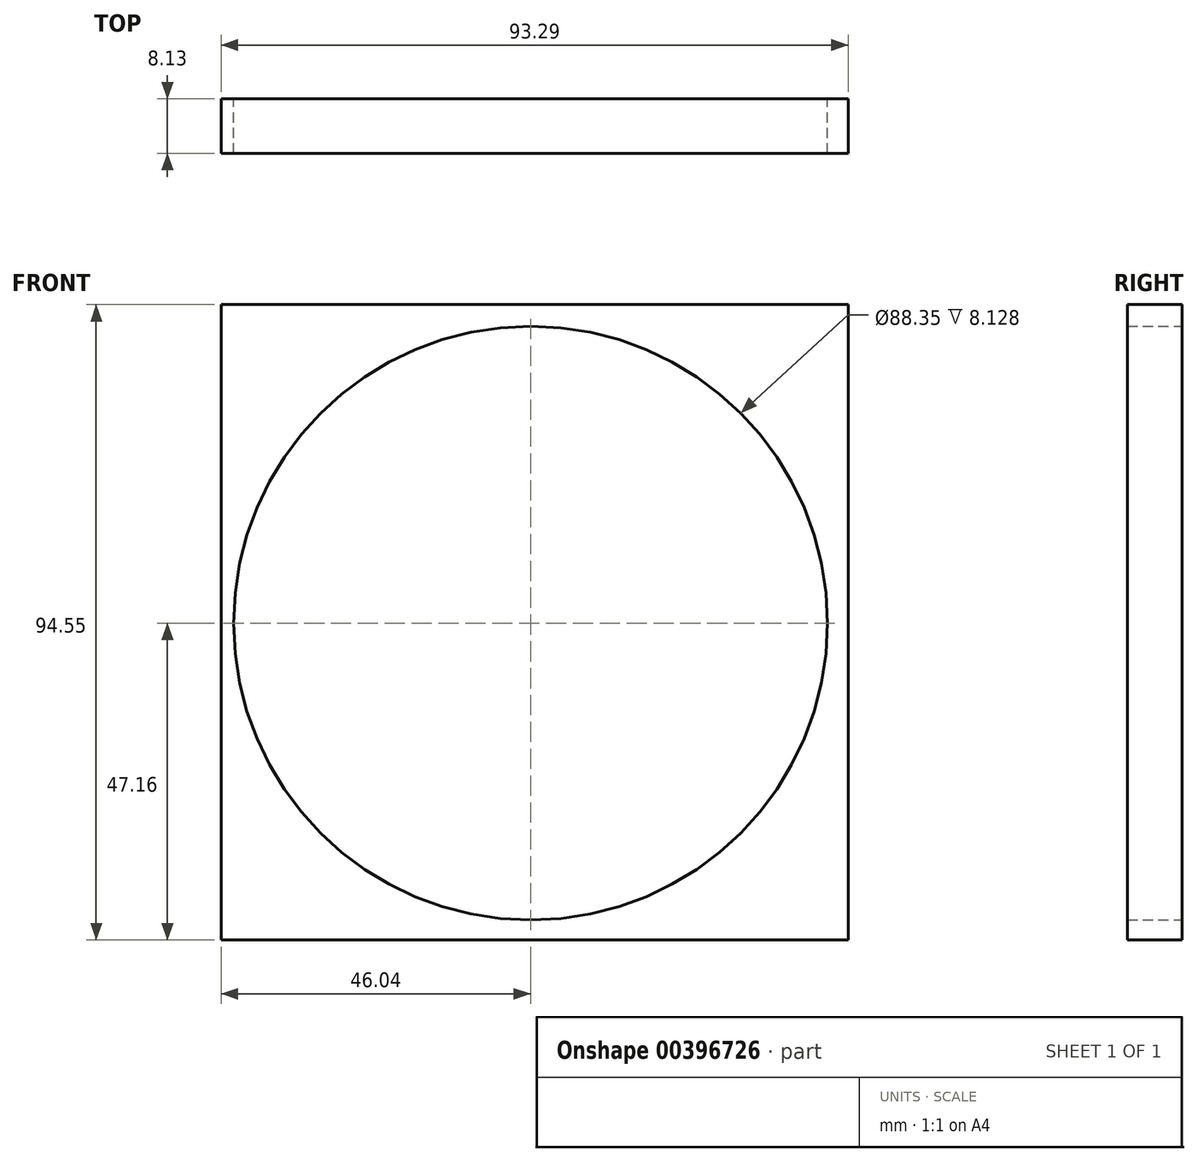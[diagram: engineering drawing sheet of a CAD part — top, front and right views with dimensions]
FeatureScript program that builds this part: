
annotation { "Feature Type Name" : "Feature", "Feature Type Description" : "" }
export const myFeature = defineFeature(function(context is Context, id is Id, definition is map)
    precondition{}
    {
        {
            var Q0;
            Q0=qCreatedBy(makeId("Front.planeOp"),FACE);
            var sketch = newSketch(context, id + "F0", { "sketchPlane" : qUnion([Q0])});
            skCircle(sketch, "E0", {"center": v(0, 0) * mm, "radius": 44.18 * mm});
            skCircle(sketch, "E1", {"center": v(0, 0) * mm, "radius": 43.1 * mm});
            skCircle(sketch, "E2", {"center": v(0, 0) * mm, "radius": 10.3 * mm});
            skCircle(sketch, "E3", {"center": v(0, 0) * mm, "radius": 4 * mm});
            skLineSegment(sketch, "E4", {"start": v(5.98, 41.68) * mm, "end": v(-21.14, 7.24) * mm});
            skLineSegment(sketch, "E5", {"start": v(-21.14, 7.24) * mm, "end": v(-38.78, 8.18) * mm});
            skLineSegment(sketch, "E6", {"start": v(-38.78, 8.18) * mm, "end": v(-5.25, -23.57) * mm});
            skLineSegment(sketch, "E7", {"start": v(-5.25, -23.57) * mm, "end": v(-7.88, -41.35) * mm});
            skLineSegment(sketch, "E8", {"start": v(-7.88, -41.35) * mm, "end": v(22.81, -4.61) * mm});
            skLineSegment(sketch, "E9", {"start": v(22.81, -4.61) * mm, "end": v(41.4, -6.92) * mm});
            skLineSegment(sketch, "E10", {"start": v(41.4, -6.92) * mm, "end": v(5.23, 24.04) * mm});
            skLineSegment(sketch, "E11", {"start": v(5.23, 24.04) * mm, "end": v(5.98, 41.68) * mm});
            skLineSegment(sketch, "E12", {"start": v(-46.04, 47.39) * mm, "end": v(-46.04, -47.16) * mm});
            skLineSegment(sketch, "E13", {"start": v(47.25, -47.16) * mm, "end": v(47.25, 47.39) * mm});
            skLineSegment(sketch, "E14", {"start": v(-46.04, 47.39) * mm, "end": v(47.25, 47.39) * mm});
            skLineSegment(sketch, "E15", {"start": v(47.25, -47.16) * mm, "end": v(-46.04, -47.16) * mm});
            skSolve(sketch);
        }
        {
            var Q0;
            Q0=makeQuery(id+"F0.imprint","IMPRINT",FACE,{"disambiguationData":[TD([[makeQuery(id+"F0.imprint","IMPRINT",EDGE,{"derivedFrom":sQuery(id+"F0.wireOp",EDGE,"E0")}),-1.0]])]});
            extrude(context, id + "F1", {"entities" : qUnion([Q0]), "depth" : 8.13 * mm});
        }
    });
